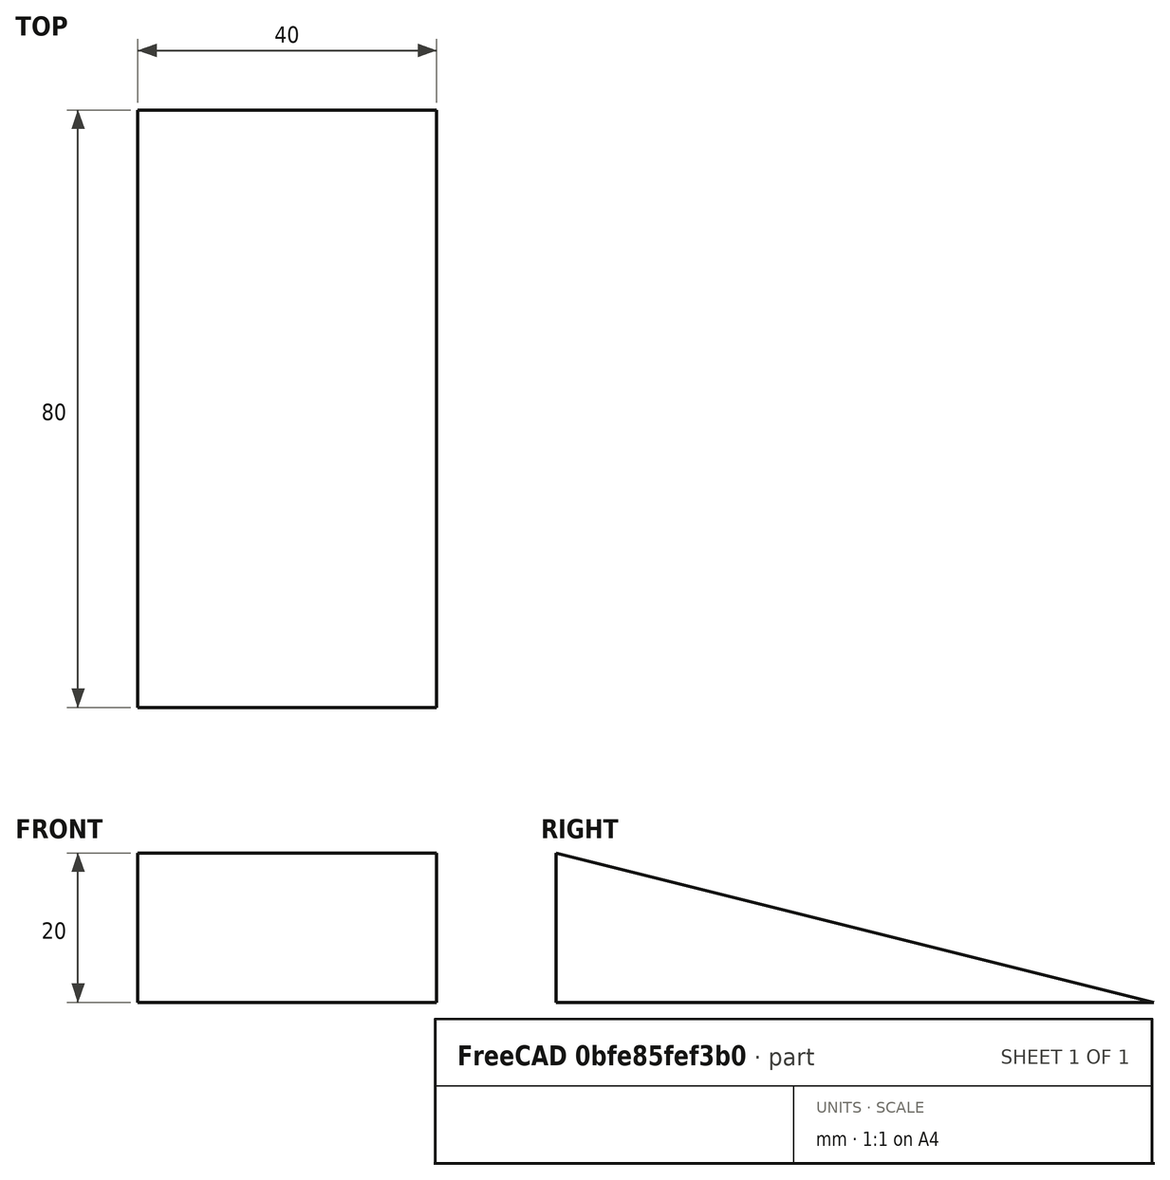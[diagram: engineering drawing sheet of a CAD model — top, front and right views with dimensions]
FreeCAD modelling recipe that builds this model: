
FCSTD DOCUMENT  (FreeCAD 0.17R13217 (Git))
Label: 07-01-calzador-puerta
License: All rights reserved
LicenseURL: http://en.wikipedia.org/wiki/All_rights_reserved
objects: TechDraw::DrawProjGroupItem×3, TechDraw::DrawViewDimension×3, Sketcher::SketchObject×1, PartDesign::Pad×1, PartDesign::Body×1, TechDraw::DrawSVGTemplate×1, TechDraw::DrawProjGroup×1, TechDraw::DrawViewPart×1, TechDraw::DrawViewAnnotation×1, TechDraw::DrawPage×1
note: 4 computed .brp shape members not serialized (recipe doc carries the construction recipe); baked Part::Feature solids carry a one-line shape summary decoded from their .brp

FEATURE [Sketcher::SketchObject] Sketch
  MapMode = 5
  Placement = pos=(0,0,0) rot=(0.57735,0.57735,0.57735;2.0944rad)
  Support = -> [YZ_Plane]
  sketch-geometry (3):
    g0: LineSegment StartX=0 StartY=0 StartZ=0 EndX=0 EndY=20 EndZ=0
    g1: LineSegment StartX=0 StartY=20 StartZ=0 EndX=80 EndY=0 EndZ=0
    g2: LineSegment StartX=80 StartY=0 StartZ=0 EndX=0 EndY=0 EndZ=0
  constraints (8):
    c: Coincident(g-1,g0)
    c: PointOnObject(g0,g-2)
    c: Coincident(g0,g1)
    c: PointOnObject(g1,g-1)
    c: Coincident(g1,g2)
    c: Coincident(g2,g0)
    c: DistanceY(g0,g0) = 20
    c: DistanceX(g2,g2) = 80
FEATURE [PartDesign::Pad] Pad
  Length = 40
  Length2 = 100
  Midplane = true
  Placement = pos=(0,0,0) rot=(0.57735,0.57735,0.57735;2.0944rad)
  Profile = -> Sketch
  Refine = true
  Type = 0
FEATURE [PartDesign::Body] Body
  Group = -> [Sketch,Pad]
  Origin = -> Origin
  Tip = -> Pad
FEATURE [TechDraw::DrawSVGTemplate] Template
  EditableTexts = Designed_by_Name=Designed by Name; Drawing_number=Drawing number; FC-Date=Date; FC-SC=Scale; FC-SH=Sheet; FC-Title=Title; Subtitle=Subtitle; Weight=Weight
  Height = 210
  Orientation = 1
  Width = 297
FEATURE [TechDraw::DrawProjGroupItem] ProjItem  label="Front"
  ArcCenterMarks = true
  CenterScale = 2
  CoarseView = false
  Direction = (0,-1,0)
  ExtraWidth = 1.4
  Focus = 100
  HardHidden = false
  HiddenWidth = 0.35
  HorizCenterLine = false
  IsoCount = 0
  IsoHidden = false
  IsoVisible = false
  IsoWidth = 0.5
  KeepLabel = false
  LineWidth = 0.7
  LockPosition = false
  Perspective = false
  Rotation = 0
  RotationVector = (1,0,0)
  ScaleType = 0
  SeamHidden = false
  SeamVisible = false
  ShowSectionLine = true
  SmoothHidden = false
  SmoothVisible = false
  Source = -> [Pad]
  Type = 0
  VertCenterLine = false
  X = 0
  Y = 62.5
FEATURE [TechDraw::DrawProjGroupItem] ProjItem001  label="Top"
  ArcCenterMarks = true
  CenterScale = 2
  CoarseView = false
  Direction = (0,0,1)
  ExtraWidth = 1.4
  Focus = 100
  HardHidden = false
  HiddenWidth = 0.35
  HorizCenterLine = false
  IsoCount = 0
  IsoHidden = false
  IsoVisible = false
  IsoWidth = 0.5
  KeepLabel = false
  LineWidth = 0.7
  LockPosition = false
  Perspective = false
  Rotation = 0
  RotationVector = (1,0,0)
  ScaleType = 0
  SeamHidden = false
  SeamVisible = false
  ShowSectionLine = true
  SmoothHidden = false
  SmoothVisible = false
  Source = -> [Pad]
  Type = 4
  VertCenterLine = false
  X = 0
  Y = -95
FEATURE [TechDraw::DrawProjGroupItem] ProjItem002  label="Left"
  ArcCenterMarks = true
  CenterScale = 2
  CoarseView = false
  Direction = (-1,0,0)
  ExtraWidth = 1.4
  Focus = 100
  HardHidden = false
  HiddenWidth = 0.35
  HorizCenterLine = false
  IsoCount = 0
  IsoHidden = false
  IsoVisible = false
  IsoWidth = 0.5
  KeepLabel = false
  LineWidth = 0.7
  LockPosition = false
  Perspective = false
  Rotation = 0
  RotationVector = (0,1,0)
  ScaleType = 0
  SeamHidden = false
  SeamVisible = false
  ShowSectionLine = true
  SmoothHidden = false
  SmoothVisible = false
  Source = -> [Pad]
  Type = 1
  VertCenterLine = false
  X = 95
  Y = 0
FEATURE [TechDraw::DrawProjGroup] ProjGroup
  Anchor = -> ProjItem
  AutoDistribute = true
  CubeDirs = (1) [(0,0,0)]
  CubeRotations = (1) [(0,0,0)]
  KeepLabel = false
  LockPosition = false
  ProjectionType = 0
  Rotation = 0
  ScaleType = 0
  Source = -> [Pad]
  Views = -> [ProjItem,ProjItem001,ProjItem002]
  X = 48.1831
  Y = 176.232
  spacingX = 15
  spacingY = 15
FEATURE [TechDraw::DrawViewPart] View
  ArcCenterMarks = true
  CenterScale = 2
  CoarseView = false
  Direction = (-1,1,1)
  ExtraWidth = 1.4
  Focus = 100
  HardHidden = false
  HiddenWidth = 0.35
  HorizCenterLine = false
  IsoCount = 0
  IsoHidden = false
  IsoVisible = false
  IsoWidth = 0.5
  KeepLabel = false
  LineWidth = 0.7
  LockPosition = false
  Perspective = false
  Rotation = 0
  ScaleType = 0
  SeamHidden = false
  SeamVisible = false
  ShowSectionLine = true
  SmoothHidden = false
  SmoothVisible = false
  Source = -> [Pad]
  VertCenterLine = false
  X = 233.042
  Y = 103.275
FEATURE [TechDraw::DrawViewAnnotation] Annotation
  Font = osifont
  KeepLabel = false
  LineSpace = 80
  LockPosition = false
  MaxWidth = -1
  Rotation = 0
  ScaleType = 0
  Text = Calzador para | puerta
  TextSize = 8
  TextStyle = 0
  X = 134.944
  Y = 102.782
FEATURE [TechDraw::DrawViewDimension] Dimension
  Font = osifont
  Fontsize = 3.5
  FormatSpec = %.2f
  KeepLabel = false
  LineWidth = 0.5
  LockPosition = false
  MeasureType = 1
  References2D = -> [ProjItem001]
  Rotation = 0
  ScaleType = 0
  Type = 2
  X = 31.7958
  Y = 0
FEATURE [TechDraw::DrawViewDimension] Dimension001
  Font = osifont
  Fontsize = 3.5
  FormatSpec = %.2f
  KeepLabel = false
  LineWidth = 0.5
  LockPosition = false
  MeasureType = 1
  References2D = -> [ProjItem001]
  Rotation = 0
  ScaleType = 0
  Type = 1
  X = -1.72535
  Y = -50.5282
FEATURE [TechDraw::DrawViewDimension] Dimension002
  Font = osifont
  Fontsize = 3.5
  FormatSpec = %.2f
  KeepLabel = false
  LineWidth = 0.5
  LockPosition = false
  MeasureType = 1
  References2D = -> [ProjItem002]
  Rotation = 0
  ScaleType = 0
  Type = 2
  X = 49.5423
  Y = -1.23239
FEATURE [TechDraw::DrawPage] Page
  KeepUpdated = true
  ProjectionType = 0
  Template = -> Template
  Views = -> [ProjGroup,View,Annotation,Dimension,Dimension001,Dimension002]
